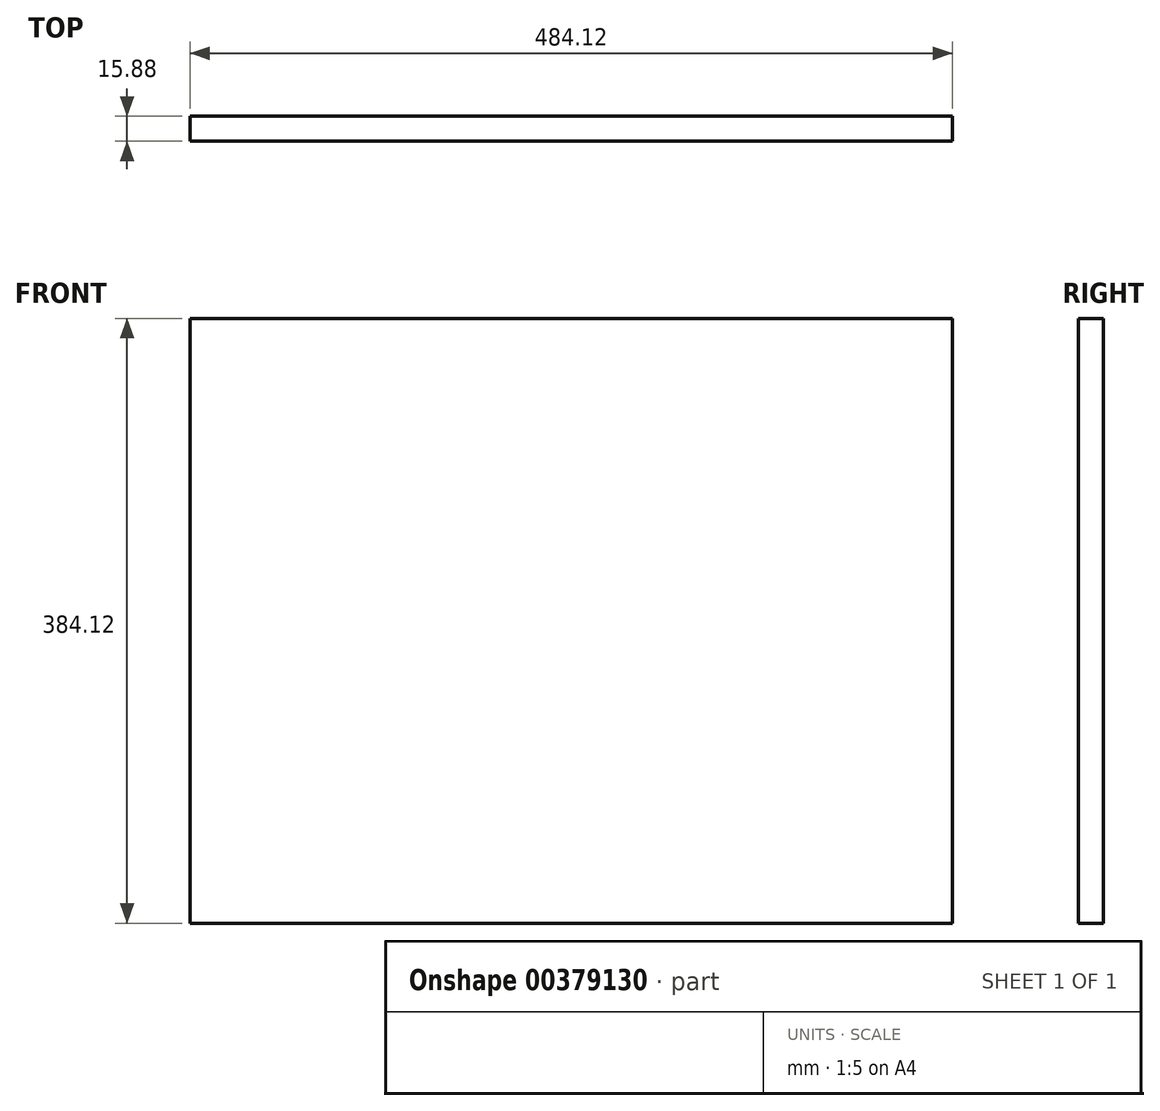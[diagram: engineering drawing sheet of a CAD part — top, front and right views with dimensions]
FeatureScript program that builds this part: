
annotation { "Feature Type Name" : "Feature", "Feature Type Description" : "" }
export const myFeature = defineFeature(function(context is Context, id is Id, definition is map)
    precondition{}
    {
        {
            var Q0;
            Q0=qCreatedBy(makeId("Front.planeOp"),FACE);
            var sketch = newSketch(context, id + "F0", { "sketchPlane" : qUnion([Q0])});
            skLineSegment(sketch, "E0.bottom", {"start": v(242.06, -192.06) * mm, "end": v(-242.06, -192.06) * mm});
            skLineSegment(sketch, "E0.top", {"start": v(242.06, 192.06) * mm, "end": v(-242.06, 192.06) * mm});
            skLineSegment(sketch, "E0.left", {"start": v(242.06, -192.06) * mm, "end": v(242.06, 192.06) * mm});
            skLineSegment(sketch, "E0.right", {"start": v(-242.06, -192.06) * mm, "end": v(-242.06, 192.06) * mm});
            skPoint(sketch, "E0.middle", {"position": v(0, 0) * mm});
            skSolve(sketch);
        }
        {
            var Q0;
            Q0=makeQuery(id+"F0.imprint","IMPRINT",FACE,{"disambiguationData":[TD([[makeQuery(id+"F0.imprint","IMPRINT",EDGE,{"derivedFrom":sQuery(id+"F0.wireOp",EDGE,"E0.bottom")}),-1.0]])]});
            extrude(context, id + "F1", {"entities" : qUnion([Q0]), "depth" : 15.88 * mm});
        }
    });
